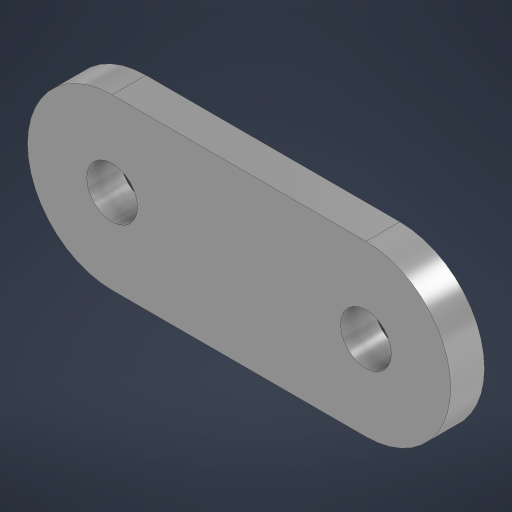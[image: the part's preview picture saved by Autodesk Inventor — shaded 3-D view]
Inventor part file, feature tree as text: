
AUTODESK INVENTOR PART (.ipt)
format: ipt  version: 2023 (Build 270158000, 158)  size: 182,272 bytes
history: native  units: mm
features: extrude x2, sketch x2, fillet x1
ambient origin geometry x8: Origin, YZ Plane, XZ Plane, XY Plane, X Axis, Y Axis, Z Axis, Center Point
bodies: Solid1 (feature_tree)
feature tree (5):
  extrude  "Extrusion1"  Depth=10.0mm
  fillet  "Fillet1"  Radius=2.0mm
  extrude  "Extrusion2"  Depth=2.0mm
  sketch  "Sketch1"  dims[d0=25.0mm d1=10.0mm d2=2.0mm d3=0.0mm]
  sketch  "Sketch2"  dims[d4=5.0mm d5=3.0mm d6=3.0mm d7=2.0mm d8=0.0mm]
